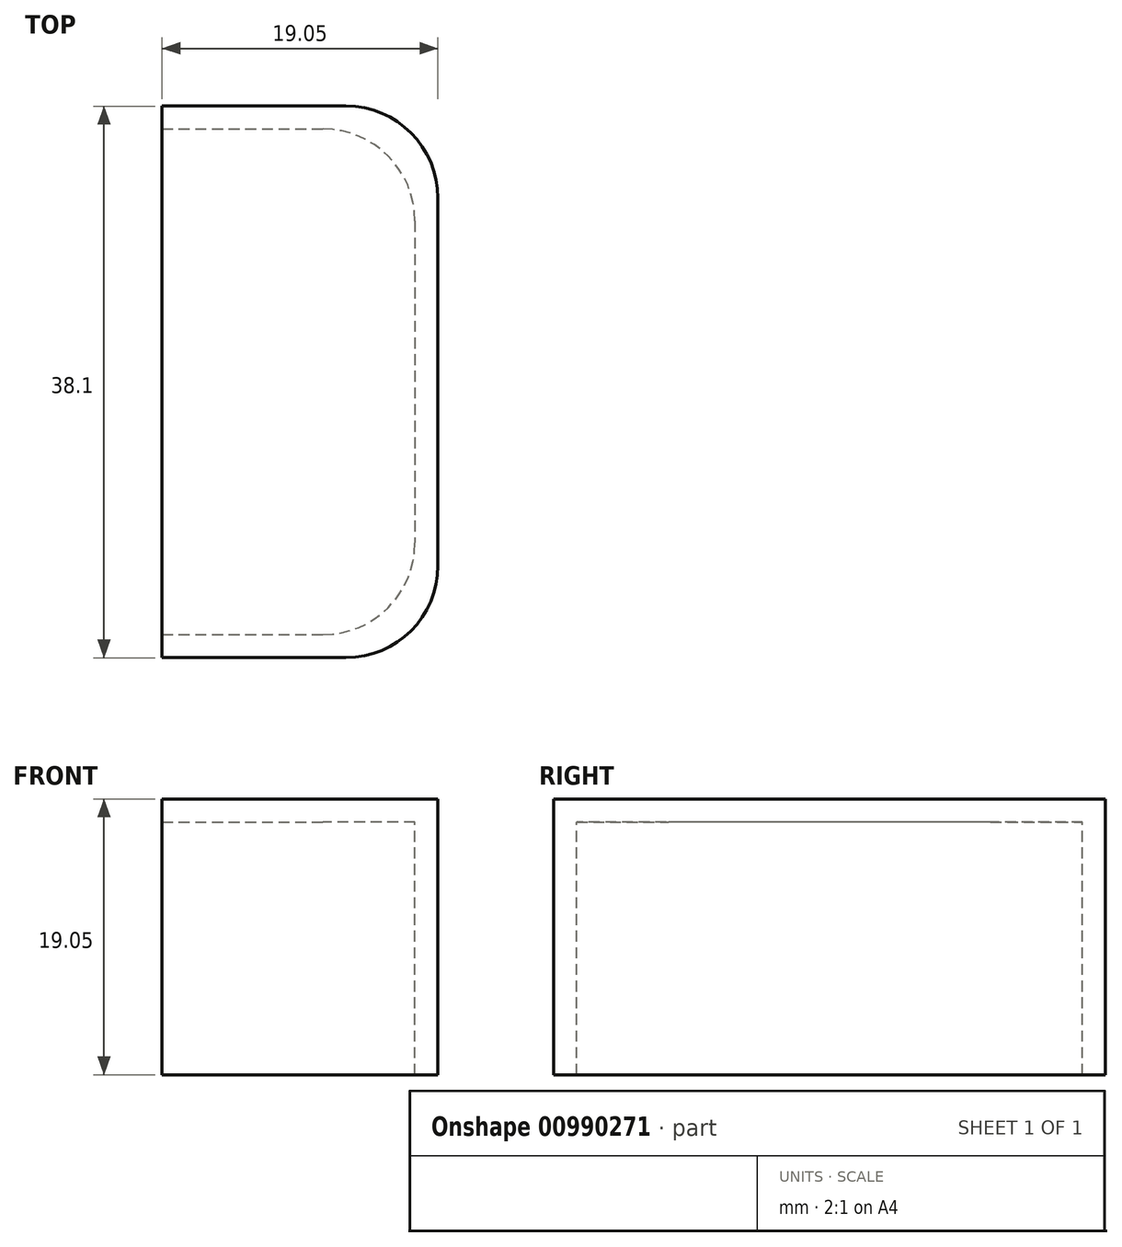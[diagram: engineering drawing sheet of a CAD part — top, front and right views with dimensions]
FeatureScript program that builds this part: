
annotation { "Feature Type Name" : "Feature", "Feature Type Description" : "" }
export const myFeature = defineFeature(function(context is Context, id is Id, definition is map)
    precondition{}
    {
        {
            var Q0;
            Q0=qCreatedBy(makeId("Top.planeOp"),FACE);
            var sketch = newSketch(context, id + "F0", { "sketchPlane" : qUnion([Q0])});
            skLineSegment(sketch, "E0.bottom", {"start": v(15.01, 15.04) * mm, "end": v(40.41, 15.04) * mm});
            skLineSegment(sketch, "E0.top", {"start": v(15.01, -23.06) * mm, "end": v(40.41, -23.06) * mm});
            skLineSegment(sketch, "E0.left", {"start": v(8.66, 8.7) * mm, "end": v(8.66, -16.7) * mm});
            skLineSegment(sketch, "E0.right", {"start": v(46.76, 8.7) * mm, "end": v(46.76, -16.7) * mm});
            skPoint(sketch, "E1.visualSharp", {"position": v(46.76, 15.04) * mm});
            skArc(sketch, "E1.filletArc", {"start": v(46.76, 8.7) * mm, "mid": v(44.9, 13.19) * mm, "end": v(40.41, 15.04) * mm});
            skPoint(sketch, "E2.visualSharp", {"position": v(8.66, 15.04) * mm});
            skArc(sketch, "E2.filletArc", {"start": v(15.01, 15.04) * mm, "mid": v(10.52, 13.19) * mm, "end": v(8.66, 8.7) * mm});
            skPoint(sketch, "E3.visualSharp", {"position": v(8.66, -23.06) * mm});
            skArc(sketch, "E3.filletArc", {"start": v(8.66, -16.7) * mm, "mid": v(10.52, -21.2) * mm, "end": v(15.01, -23.06) * mm});
            skPoint(sketch, "E4.visualSharp", {"position": v(46.76, -23.06) * mm});
            skArc(sketch, "E4.filletArc", {"start": v(40.41, -23.06) * mm, "mid": v(44.9, -21.2) * mm, "end": v(46.76, -16.7) * mm});
            skPoint(sketch, "E5", {"position": v(27.71, 15.04) * mm});
            skPoint(sketch, "E6", {"position": v(27.71, -23.06) * mm});
            skLineSegment(sketch, "E7", {"start": v(27.71, 15.04) * mm, "end": v(27.71, -23.06) * mm});
            skSolve(sketch);
        }
        {
            var Q0;
            Q0=makeQuery(id+"F0.imprint","IMPRINT",FACE,{"disambiguationData":[TD([[makeQuery(id+"F0.imprint","IMPRINT",EDGE,{"derivedFrom":sQuery(id+"F0.wireOp",EDGE,"E0.right")}),-1.0]])]});
            extrude(context, id + "F1", {"entities" : qUnion([Q0]), "depth" : 1.59 * mm, "offsetDistance" : 25.4 * mm});
        }
        {
            var Q0;
            Q0=makeQuery(id+"F1.opExtrude","CAP_FACE",FACE,{"disambiguationData":[OSD([sQuery(id+"F0.wireOp",EDGE,"E0.bottom"),sQuery(id+"F0.wireOp",EDGE,"E0.top"),sQuery(id+"F0.wireOp",EDGE,"E0.left"),sQuery(id+"F0.wireOp",EDGE,"E0.right"),sQuery(id+"F0.wireOp",EDGE,"E1.filletArc"),sQuery(id+"F0.wireOp",EDGE,"E2.filletArc"),sQuery(id+"F0.wireOp",EDGE,"E3.filletArc"),sQuery(id+"F0.wireOp",EDGE,"E4.filletArc")])],"isStart":false});
            var sketch = newSketch(context, id + "F2", { "sketchPlane" : qUnion([Q0])});
            skLineSegment(sketch, "E8.0", {"start": v(16.6, 13.46) * mm, "end": v(38.82, 13.46) * mm});
            skLineSegment(sketch, "E8.1", {"start": v(10.25, 7.1) * mm, "end": v(10.25, -15.12) * mm});
            skLineSegment(sketch, "E8.2", {"start": v(16.6, -21.47) * mm, "end": v(38.82, -21.47) * mm});
            skLineSegment(sketch, "E8.3", {"start": v(45.17, 7.1) * mm, "end": v(45.17, -15.12) * mm});
            skPoint(sketch, "E9.visualSharp", {"position": v(10.25, -21.47) * mm});
            skArc(sketch, "E9.filletArc", {"start": v(10.25, -15.12) * mm, "mid": v(12.1, -19.6) * mm, "end": v(16.6, -21.47) * mm});
            skPoint(sketch, "E10.visualSharp", {"position": v(45.17, -21.47) * mm});
            skArc(sketch, "E10.filletArc", {"start": v(38.82, -21.47) * mm, "mid": v(43.31, -19.6) * mm, "end": v(45.17, -15.12) * mm});
            skPoint(sketch, "E11.visualSharp", {"position": v(45.17, 13.46) * mm});
            skArc(sketch, "E11.filletArc", {"start": v(45.17, 7.1) * mm, "mid": v(43.31, 11.6) * mm, "end": v(38.82, 13.46) * mm});
            skPoint(sketch, "E12.visualSharp", {"position": v(10.25, 13.46) * mm});
            skArc(sketch, "E12.filletArc", {"start": v(16.6, 13.46) * mm, "mid": v(12.1, 11.6) * mm, "end": v(10.25, 7.1) * mm});
            skSolve(sketch);
        }
        {
            var Q0;
            Q0=makeQuery(id+"F2.imprint","IMPRINT",FACE,{"disambiguationData":[TD([[makeQuery(id+"F2.imprint","IMPRINT",EDGE,{"derivedFrom":sQuery(id+"F2.wireOp",EDGE,"E8.0")}),1.0]])]});
            extrude(context, id + "F3", {"entities" : qUnion([Q0]), "operationType" : NewBodyOperationType.ADD, "oppositeDirection" : true, "depth" : 19.05 * mm, "offsetDistance" : 25.4 * mm});
        }
    });
